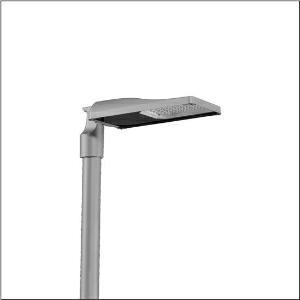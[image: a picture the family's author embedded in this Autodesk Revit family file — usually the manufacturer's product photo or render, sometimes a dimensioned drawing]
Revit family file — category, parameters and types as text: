
# Revit family: streetlight_sl_31_mini___st1_0a_5xh6d3ab08ga_4fba
name_source: partatom
category: Lighting Fixtures
units: mm (PartAtom-declared; Revit-internal decimal feet)

## family parameters
Cut with Voids When Loaded = No
Host = Face
Light Source = No
Part Type = Normal
Room Calculation Point = No
Round Connector Dimension = Use Diameter
Shared = No

## types (1)
- --- (1 x LED, 5710 lm, 37.3 W, 3000K)
    Apparent Load = 37 VA
    CIE Flux Codes = 37 72 97 100 100
    Color Rendering = 70
    Color Temperature = 3000K
    Default Elevation = 1800 mm
    Description = Streetlight SL 31 mini Easy LST mast luminaire for post-top, side-entry; light control with lens of PMMA; light distribution: ST1.0a, direct asymmetric distribution, for standard-compliant lighting for roads and squares; LED: luminous flux: 5.710lm, light colour: 730, colour temperature: 3000K; luminous efficacy: 153,1lm/W; control: pre-setting: linear dimming characteristic, flexible luminous flux parameterisation, time-dependent luminous flux control, constant luminous flux control, power reduction, intelligent temperature release in ECG and LED module, overheat protection; luminaire housing, of diecast aluminium, SITECO metallic grey (DB 702S), corrosivity category C5 high according to DIN EN ISO 12944; cover of toughened safety glass, transparent, opened without tools; mast flange of diecast aluminium, SITECO metallic grey (DB 702S), spigot size: 76/60mm, mast flange included unmounted; cable length: 6,5m, connection cable pre-assembled; mains connection: 220..240V, AC, 50/60Hz; power consumption (at start of service life): 37,3W / (at end of service life): 38,7W / (with reduced operation 50%): 17,5W; protection rating (complete): IP66; insulation class (complete): insulation class II (safety insulation); impact resistance: IK10; certification: CE, ENEC, ENEC+, VDE, UKCA; permissible operating ambient temperature for outdoor applications: -40..+50°C; packaging unit: 1 piece

Light Distribution: ST1.0a
    Height = 76 mm
    Lamp = 1 x LED
    Lamp Light Flux = 5710 lm
    Lamp Power = 37.3 W
    Lamp count = 1
    Length = 547 mm
    Luminous efficacy = 153 lm/W
    Manufacturer = Siteco
    ModVariant = No
    Model = 5XH6D3AB08GA
    Mounting Place = Pole
    Mounting Type = Pole top
    Number of Poles = 1
    OnlyDefault = Yes
    Power Factor = 1
    Product Name = Streetlight SL 31 mini | ST1.0a
    Product group = mast luminaire | pylon top
    ProductGroupID = 6100
    Protection Class = Protection class II
    Protection Degree = IP 66
    RLX_Detail_Level = 1
    RLX_Emergency_Light_Flux = 0 lm
    RLX_Emergency_Type = 0
    RLX_Emergency_Type_DB = No
    RlxData = <blob elided: 39569 chars, md5=cd3d044c>
    Socket = socket
    Standby Power = 0 W
    System Light Flux = 5710 lm
    System Power = 37 W
    Type Comments = factory setting: luminous flux: 100 % | dim-lin: 254 | 386 mA
    Type Image = l_1300326.jpg
    URL = http://relux.com
    VarID = @adj_062463
    Voltage = 0 V
    Weight = 0.00 kg
    Width = 265 mm

## geometry (parser evidence)
native form markers: Blend x4, Sweep x10
no freeform markers — native parametric forms only
